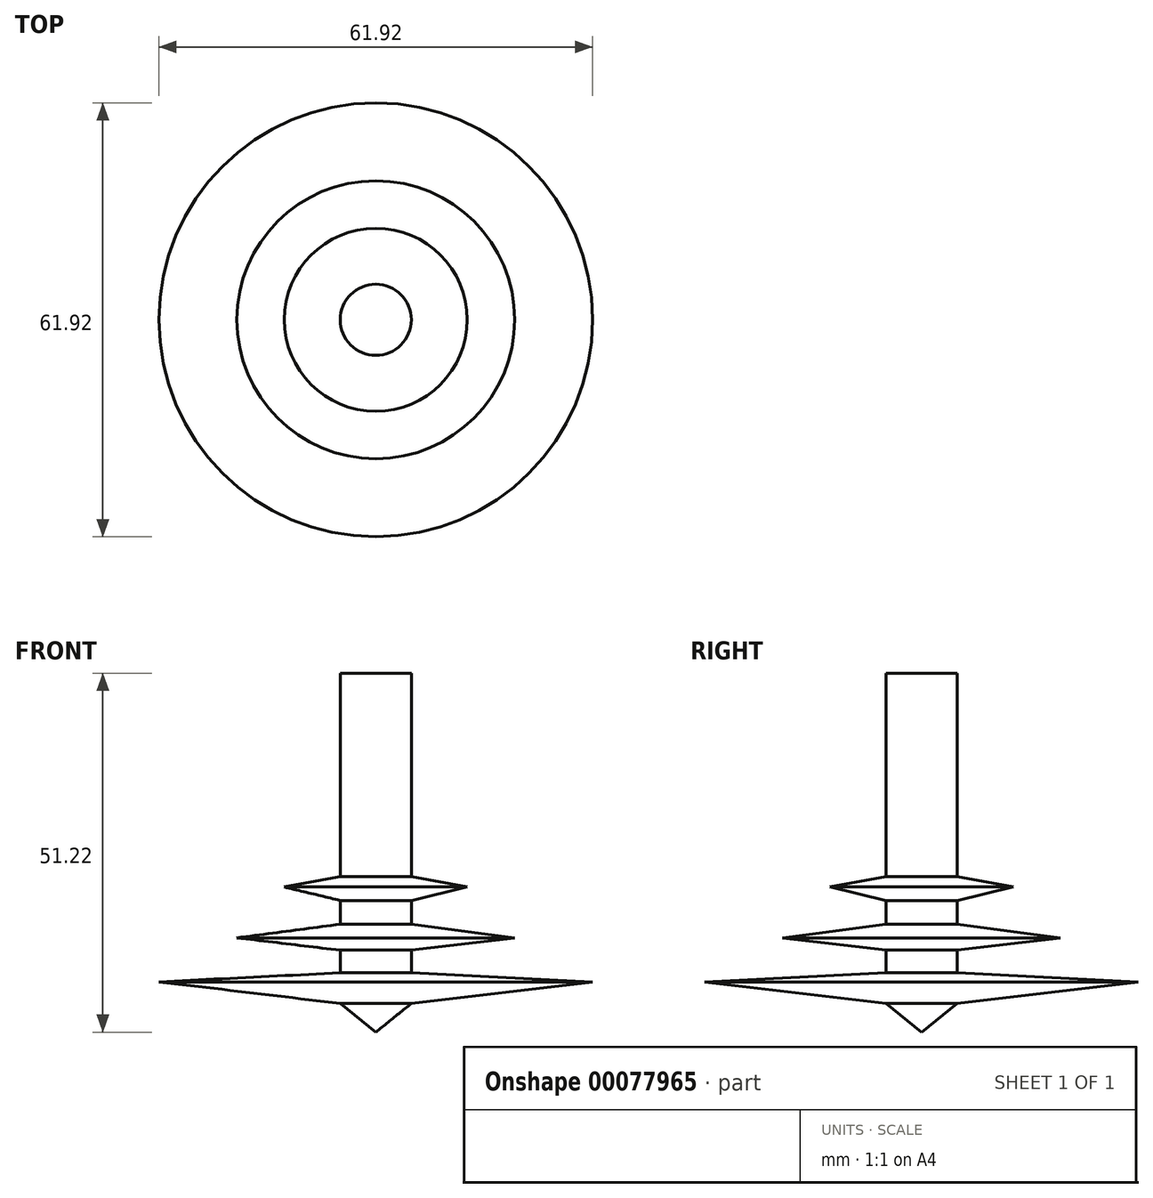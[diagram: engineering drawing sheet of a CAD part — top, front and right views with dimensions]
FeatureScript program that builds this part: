
annotation { "Feature Type Name" : "Feature", "Feature Type Description" : "" }
export const myFeature = defineFeature(function(context is Context, id is Id, definition is map)
    precondition{}
    {
        {
            var Q0;
            Q0=qCreatedBy(makeId("Front.planeOp"),FACE);
            var sketch = newSketch(context, id + "F0", { "sketchPlane" : qUnion([Q0])});
            skLineSegment(sketch, "E0", {"start": v(0, 0) * mm, "end": v(0, 51.22) * mm});
            skLineSegment(sketch, "E1", {"start": v(0, 51.22) * mm, "end": v(5.08, 51.22) * mm});
            skLineSegment(sketch, "E2", {"start": v(5.08, 4.1) * mm, "end": v(0, 0) * mm});
            skLineSegment(sketch, "E3", {"start": v(5.08, 8.47) * mm, "end": v(30.96, 7.18) * mm});
            skLineSegment(sketch, "E4", {"start": v(30.96, 7.18) * mm, "end": v(5.08, 4.1) * mm});
            skLineSegment(sketch, "E5", {"start": v(5.08, 15.4) * mm, "end": v(19.84, 13.47) * mm});
            skLineSegment(sketch, "E6", {"start": v(19.84, 13.47) * mm, "end": v(5.08, 11.7) * mm});
            skLineSegment(sketch, "E7", {"start": v(5.08, 22.17) * mm, "end": v(13.06, 20.72) * mm});
            skLineSegment(sketch, "E8", {"start": v(13.06, 20.72) * mm, "end": v(5.08, 18.79) * mm});
            skLineSegment(sketch, "E9", {"start": v(5.08, 51.22) * mm, "end": v(5.08, 22.17) * mm});
            skLineSegment(sketch, "E10", {"start": v(5.08, 18.79) * mm, "end": v(5.08, 15.4) * mm});
            skLineSegment(sketch, "E11", {"start": v(5.08, 11.7) * mm, "end": v(5.08, 8.47) * mm});
            skSolve(sketch);
        }
        {
            var Q0;
            Q0=makeQuery(id+"F0.imprint","IMPRINT",FACE,{"disambiguationData":[TD([[makeQuery(id+"F0.imprint","IMPRINT",EDGE,{"derivedFrom":sQuery(id+"F0.wireOp",EDGE,"E0")}),-1.0]])]});
            var Q1;
            Q1=sQuery(id+"F0.wireOp",EDGE,"E0");
            revolve(context, id + "F1", {"entities" : qUnion([Q0]), "axis" : qUnion([Q1]), "revolveType" : RevolveType.FULL});
        }
    });
